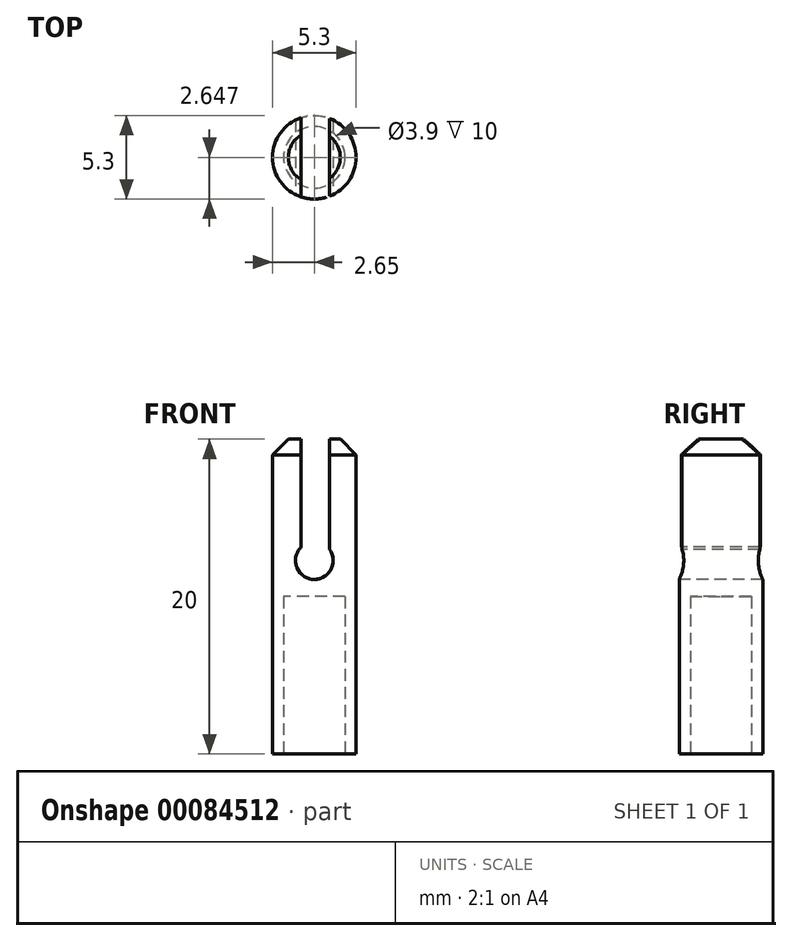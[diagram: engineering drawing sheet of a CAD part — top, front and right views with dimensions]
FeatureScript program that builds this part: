
annotation { "Feature Type Name" : "Feature", "Feature Type Description" : "" }
export const myFeature = defineFeature(function(context is Context, id is Id, definition is map)
    precondition{}
    {
        {
            var Q0;
            Q0=qCreatedBy(makeId("Top.planeOp"),FACE);
            var sketch = newSketch(context, id + "F0", { "sketchPlane" : qUnion([Q0])});
            skCircle(sketch, "E0", {"center": v(0, 0.13) * mm, "radius": 2.65 * mm});
            skCircle(sketch, "E1", {"center": v(0, 0.13) * mm, "radius": 1.95 * mm});
            skSolve(sketch);
        }
        {
            var Q0;
            Q0=makeQuery(id+"F0.imprint","IMPRINT",FACE,{"disambiguationData":[TD([[makeQuery(id+"F0.imprint","IMPRINT",EDGE,{"derivedFrom":sQuery(id+"F0.wireOp",EDGE,"E0")}),1.0]])]});
            extrude(context, id + "F1", {"entities" : qUnion([Q0]), "depth" : 10 * mm});
        }
        {
            var Q0;
            Q0=makeQuery(id+"F1.opExtrude","CAP_FACE",FACE,{"disambiguationData":[OSD([sQuery(id+"F0.wireOp",EDGE,"E0"),sQuery(id+"F0.wireOp",EDGE,"E1")])],"isStart":false});
            var sketch = newSketch(context, id + "F2", { "sketchPlane" : qUnion([Q0])});
            skCircle(sketch, "E2", {"center": v(0, 0.13) * mm, "radius": 2.65 * mm});
            skSolve(sketch);
        }
        {
            var Q0;
            Q0 = qSketchRegion(id + "F2", true);
            extrude(context, id + "F3", {"entities" : qUnion([Q0]), "operationType" : NewBodyOperationType.ADD, "depth" : 10 * mm});
        }
        {
            var Q0;
            Q0=makeQuery(id+"F3.opExtrude","CAP_EDGE",EDGE,{"disambiguationData":[OSD([sQuery(id+"F2.wireOp",EDGE,"E2")])],"isStart":false});
            chamfer(context, id + "F4", {"entities" : qUnion([Q0]), "width" : 1 * mm, "tangentPropagation" : true});
        }
        {
            var Q0;
            Q0=qCreatedBy(makeId("Front.planeOp"),FACE);
            var sketch = newSketch(context, id + "F5", { "sketchPlane" : qUnion([Q0])});
            skLineSegment(sketch, "E3.bottom", {"start": v(-0.84, 12.28) * mm, "end": v(0.96, 12.28) * mm});
            skLineSegment(sketch, "E3.top", {"start": v(-0.84, 20.02) * mm, "end": v(0.96, 20.02) * mm});
            skLineSegment(sketch, "E3.left", {"start": v(-0.84, 12.28) * mm, "end": v(-0.84, 20.02) * mm});
            skLineSegment(sketch, "E3.right", {"start": v(0.96, 12.28) * mm, "end": v(0.96, 20.02) * mm});
            skCircle(sketch, "E4", {"center": v(0, 12.28) * mm, "radius": 1.2 * mm});
            skSolve(sketch);
        }
        {
            var Q0;
            Q0 = qSketchRegion(id + "F5", true);
            extrude(context, id + "F6", {"entities" : qUnion([Q0]), "operationType" : NewBodyOperationType.REMOVE, "endBound" : BoundingType.THROUGH_ALL, "oppositeDirection" : true, "depth" : 25 * mm});
        }
        {
            var Q0;
            Q0=makeQuery(id+"F6.boolean.opBoolean","COPY",FACE,{"derivedFrom":makeQuery(id+"F6.opExtrude","CAP_FACE",FACE,{"disambiguationData":[OSD([sQuery(id+"F5.wireOp",EDGE,"E3.top"),sQuery(id+"F5.wireOp",EDGE,"E3.left"),sQuery(id+"F5.wireOp",EDGE,"E3.right"),sQuery(id+"F5.wireOp",EDGE,"E4")])],"isStart":true})});
            extrude(context, id + "F7", {"entities" : qUnion([Q0]), "operationType" : NewBodyOperationType.REMOVE, "endBound" : BoundingType.THROUGH_ALL, "oppositeDirection" : true, "depth" : 25 * mm});
        }
    });
